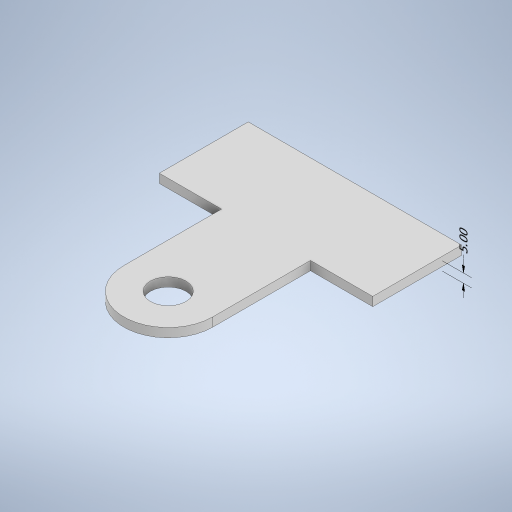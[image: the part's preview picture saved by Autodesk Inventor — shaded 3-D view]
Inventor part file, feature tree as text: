
AUTODESK INVENTOR PART (.ipt)
format: ipt  version: 2024.1 (Build 281209000, 209)  size: 256,000 bytes
history: native  units: mm
features: other x2, extrude x2, sketch x2
ambient origin geometry x8: Origin, YZ Plane, XZ Plane, XY Plane, X Axis, Y Axis, Z Axis, Center Point
bodies: Body1 (feature_tree)
feature tree (6):
  other  "ソリッド1"
  extrude  "押し出し1"  Depth=114.0mm
  extrude  "押し出し4"  Depth=150.0mm
  sketch  "スケッチ1"
  sketch  "スケッチ4"
  other  "長さ寸法 2"
